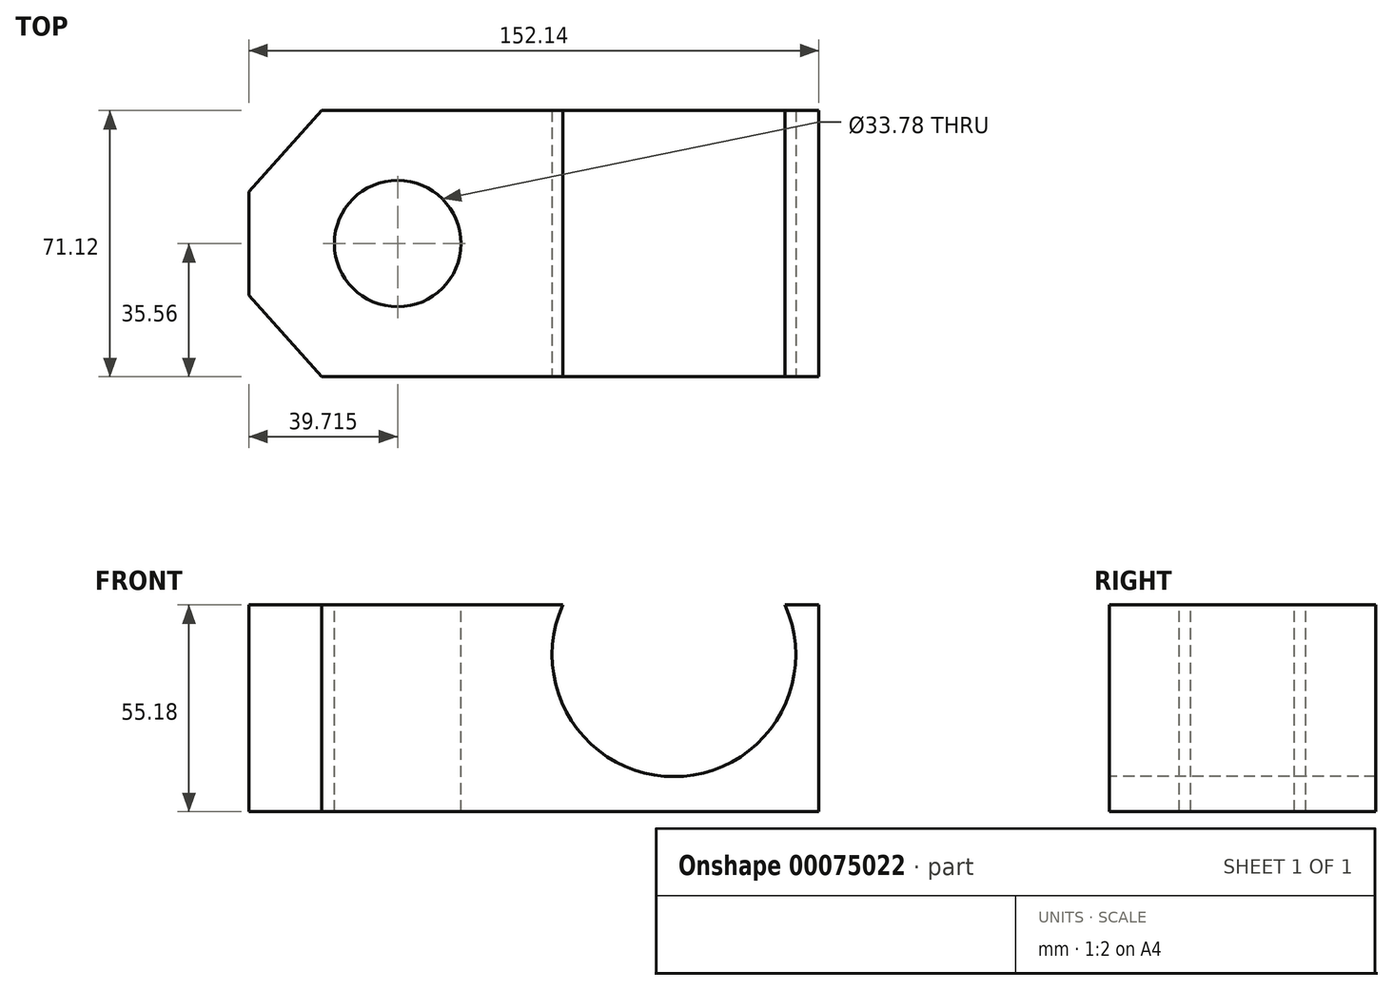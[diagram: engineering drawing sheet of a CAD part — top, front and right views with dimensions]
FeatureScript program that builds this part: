
annotation { "Feature Type Name" : "Feature", "Feature Type Description" : "" }
export const myFeature = defineFeature(function(context is Context, id is Id, definition is map)
    precondition{}
    {
        {
            var Q0;
            Q0=qCreatedBy(makeId("Front.planeOp"),FACE);
            var sketch = newSketch(context, id + "F0", { "sketchPlane" : qUnion([Q0])});
            skLineSegment(sketch, "E0.rect.bottom", {"start": v(76.07, 27.59) * mm, "end": v(-76.07, 27.59) * mm});
            skLineSegment(sketch, "E0.rect.top", {"start": v(76.07, -27.59) * mm, "end": v(-76.07, -27.59) * mm});
            skLineSegment(sketch, "E0.rect.left", {"start": v(76.07, 27.59) * mm, "end": v(76.07, -27.59) * mm});
            skLineSegment(sketch, "E0.rect.right", {"start": v(-76.07, 27.59) * mm, "end": v(-76.07, -27.59) * mm});
            skPoint(sketch, "E0.rect.middle", {"position": v(0, 0) * mm});
            skSolve(sketch);
        }
        {
            var Q0;
            Q0 = qSketchRegion(id + "F0", true);
            extrude(context, id + "F1", {"entities" : qUnion([Q0]), "depth" : 35.56 * mm, "hasSecondDirection" : true, "secondDirectionOppositeDirection" : true, "secondDirectionDepth" : 35.56 * mm});
        }
        {
            var Q0;
            Q0=makeQuery(id+"F1.opExtrude","CAP_FACE",FACE,{"disambiguationData":[OSD([sQuery(id+"F0.wireOp",EDGE,"E0.rect.bottom"),sQuery(id+"F0.wireOp",EDGE,"E0.rect.top"),sQuery(id+"F0.wireOp",EDGE,"E0.rect.left"),sQuery(id+"F0.wireOp",EDGE,"E0.rect.right")])],"isStart":false});
            var sketch = newSketch(context, id + "F2", { "sketchPlane" : qUnion([Q0])});
            skCircle(sketch, "E1", {"center": v(37.4, 14.29) * mm, "radius": 32.54 * mm});
            skPoint(sketch, "E1.first.point", {"position": v(7.7, 27.59) * mm});
            skPoint(sketch, "E1.second.point", {"position": v(67.09, 27.59) * mm});
            skPoint(sketch, "E1.third.point", {"position": v(47.66, -16.59) * mm});
            skSolve(sketch);
        }
        {
            var Q0;
            Q0 = qSketchRegion(id + "F2", true);
            extrude(context, id + "F3", {"entities" : qUnion([Q0]), "operationType" : NewBodyOperationType.REMOVE, "oppositeDirection" : true, "depth" : 74.66 * mm});
        }
        {
            var Q0;
            {var subQ0=sQuery(id+"F0.wireOp",EDGE,"E0.rect.right");var subQ3=sQuery(id+"F0.wireOp",EDGE,"E0.rect.bottom");Q0=makeQuery(id+"F3.boolean.opBoolean","SPLIT",FACE,{"disambiguationData":[TD([makeQuery(id+"F1.opExtrude","SWEPT_FACE",FACE,{"disambiguationData":[OSD([subQ0])]})])],"derivedFrom":makeQuery(id+"F1.opExtrude","SWEPT_FACE",FACE,{"disambiguationData":[OSD([subQ3])]})});}
            var sketch = newSketch(context, id + "F4", { "sketchPlane" : qUnion([Q0])});
            skCircle(sketch, "E2", {"center": v(-36.35, 0) * mm, "radius": 16.9 * mm});
            skSolve(sketch);
        }
        {
            var Q0;
            Q0 = qSketchRegion(id + "F4", true);
            extrude(context, id + "F5", {"entities" : qUnion([Q0]), "operationType" : NewBodyOperationType.REMOVE, "oppositeDirection" : true, "depth" : 60.75 * mm});
        }
        {
            var Q0;
            {var subQ0=sQuery(id+"F0.wireOp",EDGE,"E0.rect.right");var subQ3=sQuery(id+"F0.wireOp",EDGE,"E0.rect.bottom");Q0=makeQuery(id+"F3.boolean.opBoolean","SPLIT",FACE,{"disambiguationData":[TD([makeQuery(id+"F1.opExtrude","SWEPT_FACE",FACE,{"disambiguationData":[OSD([subQ0])]})])],"derivedFrom":makeQuery(id+"F1.opExtrude","SWEPT_FACE",FACE,{"disambiguationData":[OSD([subQ3])]})});}
            var sketch = newSketch(context, id + "F6", { "sketchPlane" : qUnion([Q0])});
            skLineSegment(sketch, "E3", {"start": v(-76.07, -35.56) * mm, "end": v(-56.62, -35.56) * mm});
            skLineSegment(sketch, "E4", {"start": v(-56.62, -35.56) * mm, "end": v(-76.07, -13.86) * mm});
            skLineSegment(sketch, "E5", {"start": v(-76.07, -13.86) * mm, "end": v(-76.07, -35.56) * mm});
            skLineSegment(sketch, "E6.MirrorCS", {"start": v(-56.62, 35.56) * mm, "end": v(-76.07, 13.86) * mm});
            skLineSegment(sketch, "E7.MirrorCS", {"start": v(-76.07, 35.56) * mm, "end": v(-56.62, 35.56) * mm});
            skLineSegment(sketch, "E8.MirrorCS", {"start": v(-76.07, 13.86) * mm, "end": v(-76.07, 35.56) * mm});
            skSolve(sketch);
        }
        {
            var Q0;
            Q0 = qSketchRegion(id + "F6", true);
            extrude(context, id + "F7", {"entities" : qUnion([Q0]), "operationType" : NewBodyOperationType.REMOVE, "oppositeDirection" : true, "depth" : 58.4 * mm});
        }
    });
